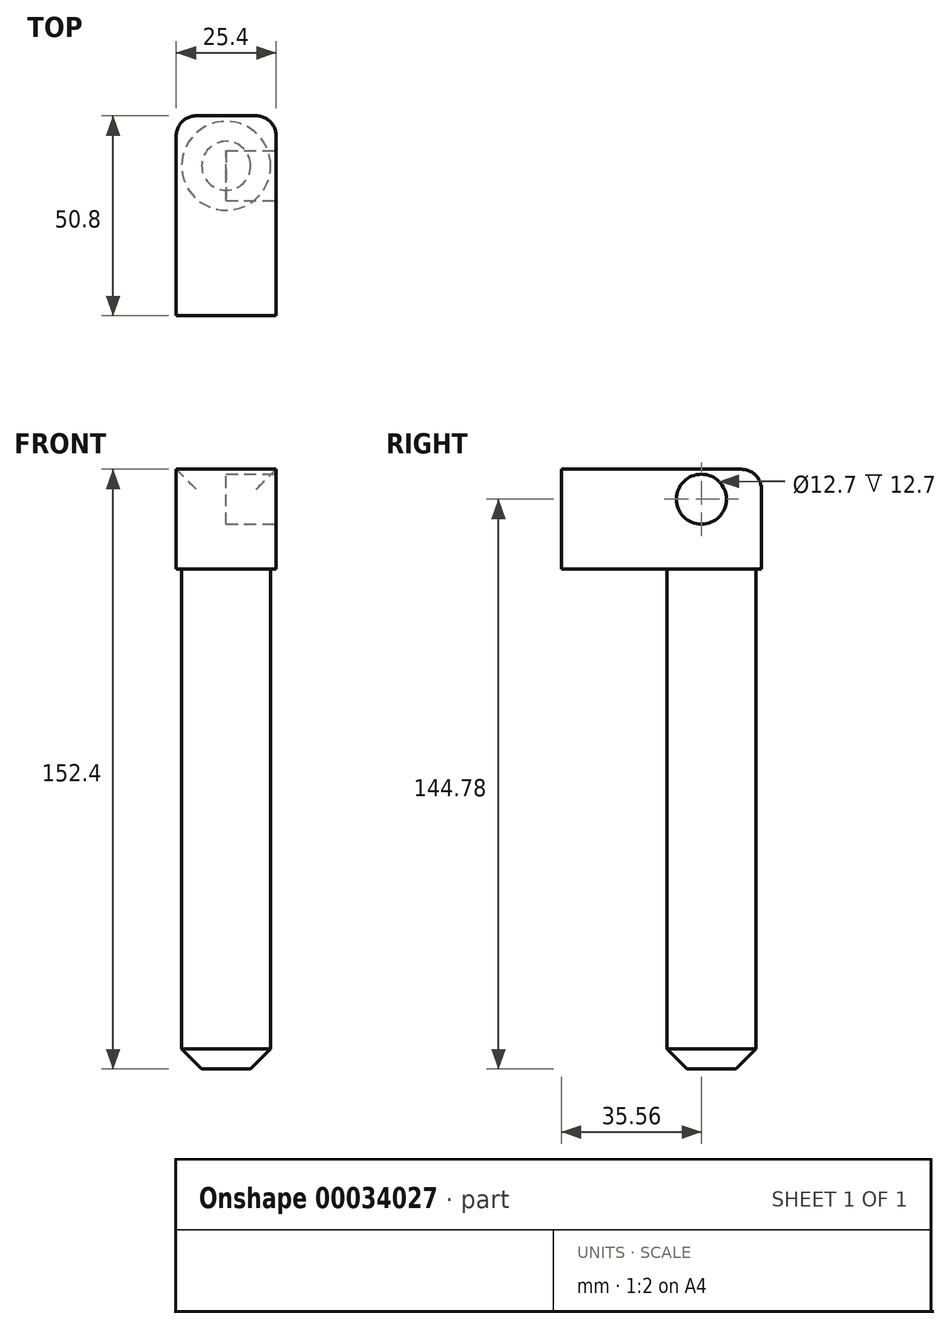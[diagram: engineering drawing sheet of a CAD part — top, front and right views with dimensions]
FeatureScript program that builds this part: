
annotation { "Feature Type Name" : "Feature", "Feature Type Description" : "" }
export const myFeature = defineFeature(function(context is Context, id is Id, definition is map)
    precondition{}
    {
        {
            var Q0;
            Q0=qCreatedBy(makeId("Top.planeOp"),FACE);
            var sketch = newSketch(context, id + "F0", { "sketchPlane" : qUnion([Q0])});
            skLineSegment(sketch, "E0.bottom", {"start": v(0, 0) * mm, "end": v(25.4, 0) * mm});
            skLineSegment(sketch, "E0.top", {"start": v(0, -50.8) * mm, "end": v(25.4, -50.8) * mm});
            skLineSegment(sketch, "E0.left", {"start": v(0, 0) * mm, "end": v(0, -50.8) * mm});
            skLineSegment(sketch, "E0.right", {"start": v(25.4, 0) * mm, "end": v(25.4, -50.8) * mm});
            skSolve(sketch);
        }
        {
            var Q0;
            Q0=makeQuery(id+"F0.imprint","IMPRINT",FACE,{"disambiguationData":[TD([[makeQuery(id+"F0.imprint","IMPRINT",EDGE,{"derivedFrom":sQuery(id+"F0.wireOp",EDGE,"E0.bottom")}),-1.0]])]});
            extrude(context, id + "F1", {"entities" : qUnion([Q0]), "depth" : 25.4 * mm});
        }
        {
            var Q0;
            Q0=makeQuery(id+"F1.opExtrude","CAP_EDGE",EDGE,{"disambiguationData":[OSD([sQuery(id+"F0.wireOp",EDGE,"E0.bottom")])],"isStart":false});
            var Q1;
            Q1=makeQuery(id+"F1.opExtrude","SWEPT_EDGE",EDGE,{"disambiguationData":[OSD([sQuery(id+"F0.wireOp",EDGE,"E0.bottom"),sQuery(id+"F0.wireOp",EDGE,"E0.right")])]});
            var Q2;
            Q2=makeQuery(id+"F1.opExtrude","SWEPT_EDGE",EDGE,{"disambiguationData":[OSD([sQuery(id+"F0.wireOp",EDGE,"E0.bottom"),sQuery(id+"F0.wireOp",EDGE,"E0.left")])]});
            fillet(context, id + "F2", {"entities" : qUnion([Q0, Q1, Q2]), "radius" : 5.08 * mm, "tangentPropagation" : true, "allowEdgeOverflow" : false});
        }
        {
            var Q0;
            Q0=makeQuery(id+"F1.opExtrude","CAP_FACE",FACE,{"disambiguationData":[OSD([sQuery(id+"F0.wireOp",EDGE,"E0.bottom"),sQuery(id+"F0.wireOp",EDGE,"E0.top"),sQuery(id+"F0.wireOp",EDGE,"E0.left"),sQuery(id+"F0.wireOp",EDGE,"E0.right")])],"isStart":true});
            var sketch = newSketch(context, id + "F3", { "sketchPlane" : qUnion([Q0])});
            skLineSegment(sketch, "E1", {"start": v(0, 0) * mm, "end": v(12.7, 0) * mm});
            skLineSegment(sketch, "E2", {"start": v(0, 0) * mm, "end": v(0, 12.7) * mm});
            skCircle(sketch, "E3", {"center": v(12.7, 12.7) * mm, "radius": 11.3 * mm});
            skSolve(sketch);
        }
        {
            var Q0;
            Q0=makeQuery(id+"F3.imprint","IMPRINT",FACE,{"disambiguationData":[TD([[makeQuery(id+"F3.imprint","IMPRINT",EDGE,{"derivedFrom":sQuery(id+"F3.wireOp",EDGE,"E3")}),1.0]])]});
            extrude(context, id + "F4", {"entities" : qUnion([Q0]), "operationType" : NewBodyOperationType.ADD, "depth" : 127 * mm});
        }
        {
            var Q0;
            Q0=makeQuery(id+"F4.opExtrude","CAP_EDGE",EDGE,{"disambiguationData":[OSD([sQuery(id+"F3.wireOp",EDGE,"E3")])],"isStart":false});
            chamfer(context, id + "F5", {"entities" : qUnion([Q0]), "width" : 5.08 * mm, "tangentPropagation" : true});
        }
        {
            var Q0;
            Q0=makeQuery(id+"F1.opExtrude","SWEPT_FACE",FACE,{"disambiguationData":[OSD([sQuery(id+"F0.wireOp",EDGE,"E0.right")])]});
            var sketch = newSketch(context, id + "F6", { "sketchPlane" : qUnion([Q0])});
            skLineSegment(sketch, "E4", {"start": v(0, 0) * mm, "end": v(0, 17.78) * mm});
            skLineSegment(sketch, "E5", {"start": v(0, 0) * mm, "end": v(-15.24, 0) * mm});
            skCircle(sketch, "E6", {"center": v(-15.24, 17.78) * mm, "radius": 6.35 * mm});
            skSolve(sketch);
        }
        {
            var Q0;
            Q0=makeQuery(id+"F6.imprint","IMPRINT",FACE,{"disambiguationData":[TD([[makeQuery(id+"F6.imprint","IMPRINT",EDGE,{"derivedFrom":sQuery(id+"F6.wireOp",EDGE,"E6")}),1.0]])]});
            extrude(context, id + "F7", {"entities" : qUnion([Q0]), "operationType" : NewBodyOperationType.REMOVE, "oppositeDirection" : true, "depth" : 12.7 * mm});
        }
    });
